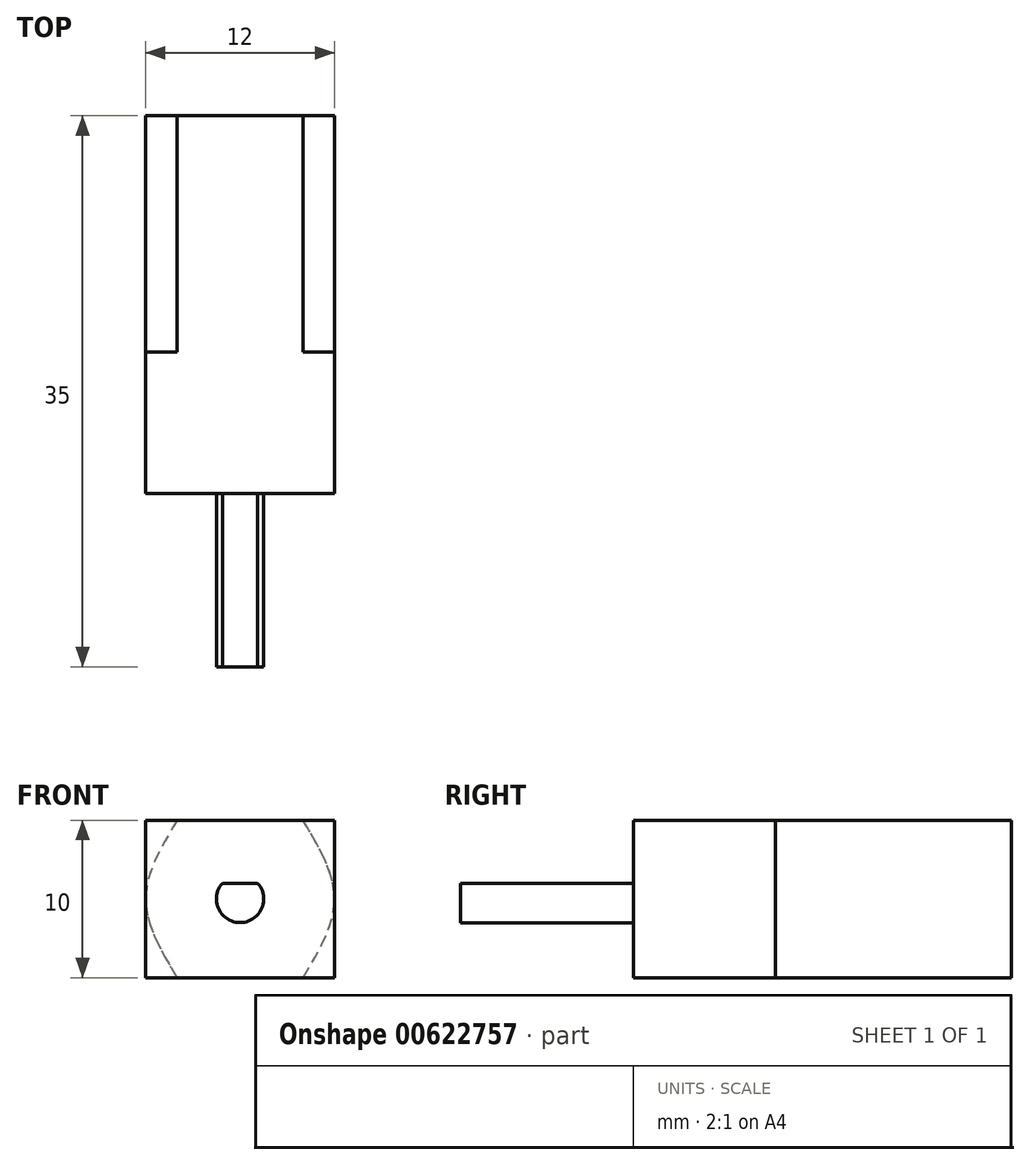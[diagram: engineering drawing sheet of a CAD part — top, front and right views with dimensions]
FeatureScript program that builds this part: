
annotation { "Feature Type Name" : "Feature", "Feature Type Description" : "" }
export const myFeature = defineFeature(function(context is Context, id is Id, definition is map)
    precondition{}
    {
        {
            var Q0;
            Q0=qCreatedBy(makeId("Front.planeOp"),FACE);
            var sketch = newSketch(context, id + "F0", { "sketchPlane" : qUnion([Q0])});
            skLineSegment(sketch, "E0.bottom", {"start": v(0, 0) * mm, "end": v(12, 0) * mm});
            skLineSegment(sketch, "E0.top", {"start": v(0, 10) * mm, "end": v(12, 10) * mm});
            skLineSegment(sketch, "E0.left", {"start": v(0, 0) * mm, "end": v(0, 10) * mm});
            skLineSegment(sketch, "E0.right", {"start": v(12, 0) * mm, "end": v(12, 10) * mm});
            skSolve(sketch);
        }
        {
            var Q0;
            Q0=makeQuery(id+"F0.imprint","IMPRINT",FACE,{"disambiguationData":[TD([[makeQuery(id+"F0.imprint","IMPRINT",EDGE,{"derivedFrom":sQuery(id+"F0.wireOp",EDGE,"E0.bottom")}),1.0]])]});
            extrude(context, id + "F1", {"entities" : qUnion([Q0]), "depth" : 9 * mm, "offsetDistance" : 25.4 * mm});
        }
        {
            var Q0;
            Q0=makeQuery(id+"F1.opExtrude","CAP_FACE",FACE,{"disambiguationData":[OSD([sQuery(id+"F0.wireOp",EDGE,"E0.bottom"),sQuery(id+"F0.wireOp",EDGE,"E0.top"),sQuery(id+"F0.wireOp",EDGE,"E0.left"),sQuery(id+"F0.wireOp",EDGE,"E0.right")])],"isStart":true});
            var sketch = newSketch(context, id + "F2", { "sketchPlane" : qUnion([Q0])});
            skLineSegment(sketch, "E1", {"start": v(-10, 10) * mm, "end": v(-2, 10) * mm});
            skLineSegment(sketch, "E2", {"start": v(-10, 0) * mm, "end": v(-2, 0) * mm});
            skFitSpline(sketch, "E3", {"points": [v(-10, 0) * mm, v(-12, 5) * mm, v(-10, 10) * mm], "startDerivative": vector(-6, 10) * mm, "endDerivative": vector(6, 10) * mm});
            skFitSpline(sketch, "E4", {"points": [v(-2, 10) * mm, v(0, 5) * mm, v(-2, 0) * mm], "startDerivative": vector(6, -10) * mm, "endDerivative": vector(-6, -10) * mm});
            skPoint(sketch, "E5.orphan", {"position": v(-12, 10) * mm});
            skPoint(sketch, "E6.orphan", {"position": v(-12, 0) * mm});
            skSolve(sketch);
        }
        {
            var Q0;
            {var subQ1=sQuery(id+"F2.wireOp",EDGE,"E1");Q0=makeQuery(id+"F2.imprint","IMPRINT",FACE,{"disambiguationData":[TD([[makeQuery(id+"F2.imprint","IMPRINT",EDGE,{"derivedFrom":subQ1}),1.0]])]});}
            extrude(context, id + "F3", {"entities" : qUnion([Q0]), "operationType" : NewBodyOperationType.ADD, "depth" : 15 * mm, "offsetDistance" : 25.4 * mm});
        }
        {
            var Q0;
            Q0=makeQuery(id+"F1.opExtrude","CAP_FACE",FACE,{"disambiguationData":[OSD([sQuery(id+"F0.wireOp",EDGE,"E0.bottom"),sQuery(id+"F0.wireOp",EDGE,"E0.top"),sQuery(id+"F0.wireOp",EDGE,"E0.left"),sQuery(id+"F0.wireOp",EDGE,"E0.right")])],"isStart":false});
            var sketch = newSketch(context, id + "F4", { "sketchPlane" : qUnion([Q0])});
            skArc(sketch, "E7", {"start": v(4.88, 6) * mm, "mid": v(6, 3.5) * mm, "end": v(7.12, 6) * mm});
            skLineSegment(sketch, "E8", {"start": v(6, 5) * mm, "end": v(6, 6) * mm});
            skLineSegment(sketch, "E9", {"start": v(6, 6) * mm, "end": v(7.12, 6) * mm});
            skLineSegment(sketch, "E10", {"start": v(6, 6) * mm, "end": v(4.88, 6) * mm});
            skSolve(sketch);
        }
        {
            var Q0;
            Q0=makeQuery(id+"F4.imprint","IMPRINT",FACE,{"disambiguationData":[TD([[makeQuery(id+"F4.imprint","IMPRINT",EDGE,{"derivedFrom":sQuery(id+"F4.wireOp",EDGE,"E7")}),1.0]])]});
            extrude(context, id + "F5", {"entities" : qUnion([Q0]), "operationType" : NewBodyOperationType.ADD, "depth" : 11 * mm, "offsetDistance" : 25.4 * mm});
        }
    });
